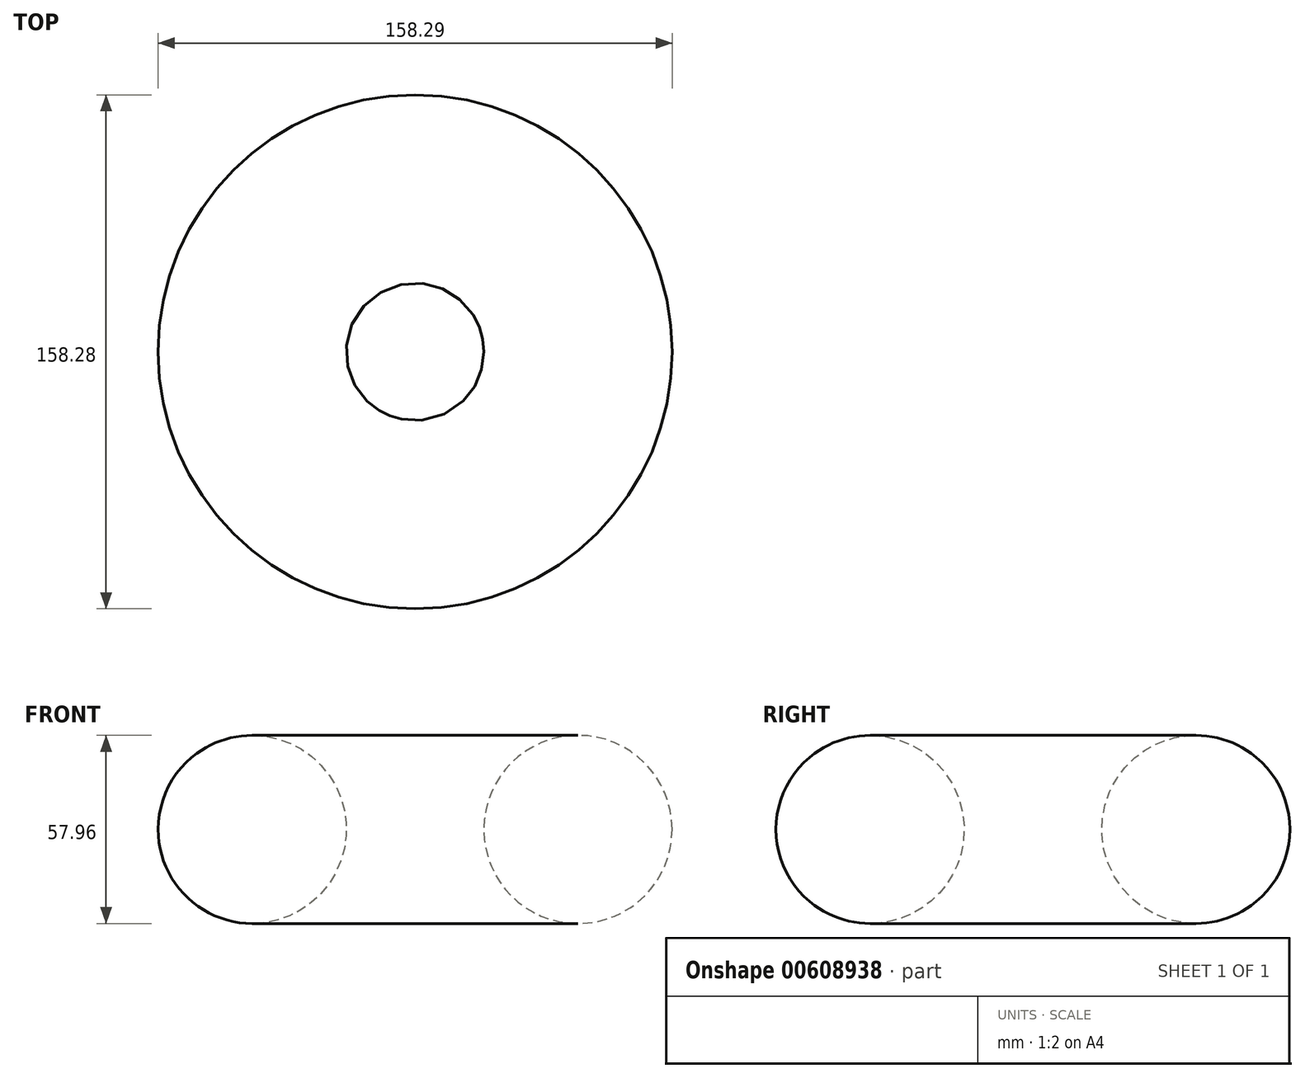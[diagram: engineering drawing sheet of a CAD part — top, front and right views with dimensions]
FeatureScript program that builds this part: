
annotation { "Feature Type Name" : "Feature", "Feature Type Description" : "" }
export const myFeature = defineFeature(function(context is Context, id is Id, definition is map)
    precondition{}
    {
        {
            var Q0;
            Q0=qCreatedBy(makeId("Front.planeOp"),FACE);
            var sketch = newSketch(context, id + "F0", { "sketchPlane" : qUnion([Q0])});
            skCircle(sketch, "E0", {"center": v(14.98, 31.04) * mm, "radius": 28.98 * mm});
            skSolve(sketch);
        }
        {
            var Q0;
            Q0=qCreatedBy(makeId("Front.planeOp"),FACE);
            var sketch = newSketch(context, id + "F1", { "sketchPlane" : qUnion([Q0])});
            skLineSegment(sketch, "E1", {"start": v(-35.19, 58.64) * mm, "end": v(-35.19, -25.26) * mm});
            skSolve(sketch);
        }
        {
            var Q0;
            Q0=makeQuery(id+"F0.imprint","IMPRINT",FACE,{"disambiguationData":[TD([[makeQuery(id+"F0.imprint","IMPRINT",EDGE,{"derivedFrom":sQuery(id+"F0.wireOp",EDGE,"E0")}),1.0]])]});
            var Q1;
            Q1=sQuery(id+"F1.wireOp",EDGE,"E1");
            revolve(context, id + "F2", {"entities" : qUnion([Q0]), "axis" : qUnion([Q1]), "revolveType" : RevolveType.FULL});
        }
    });
